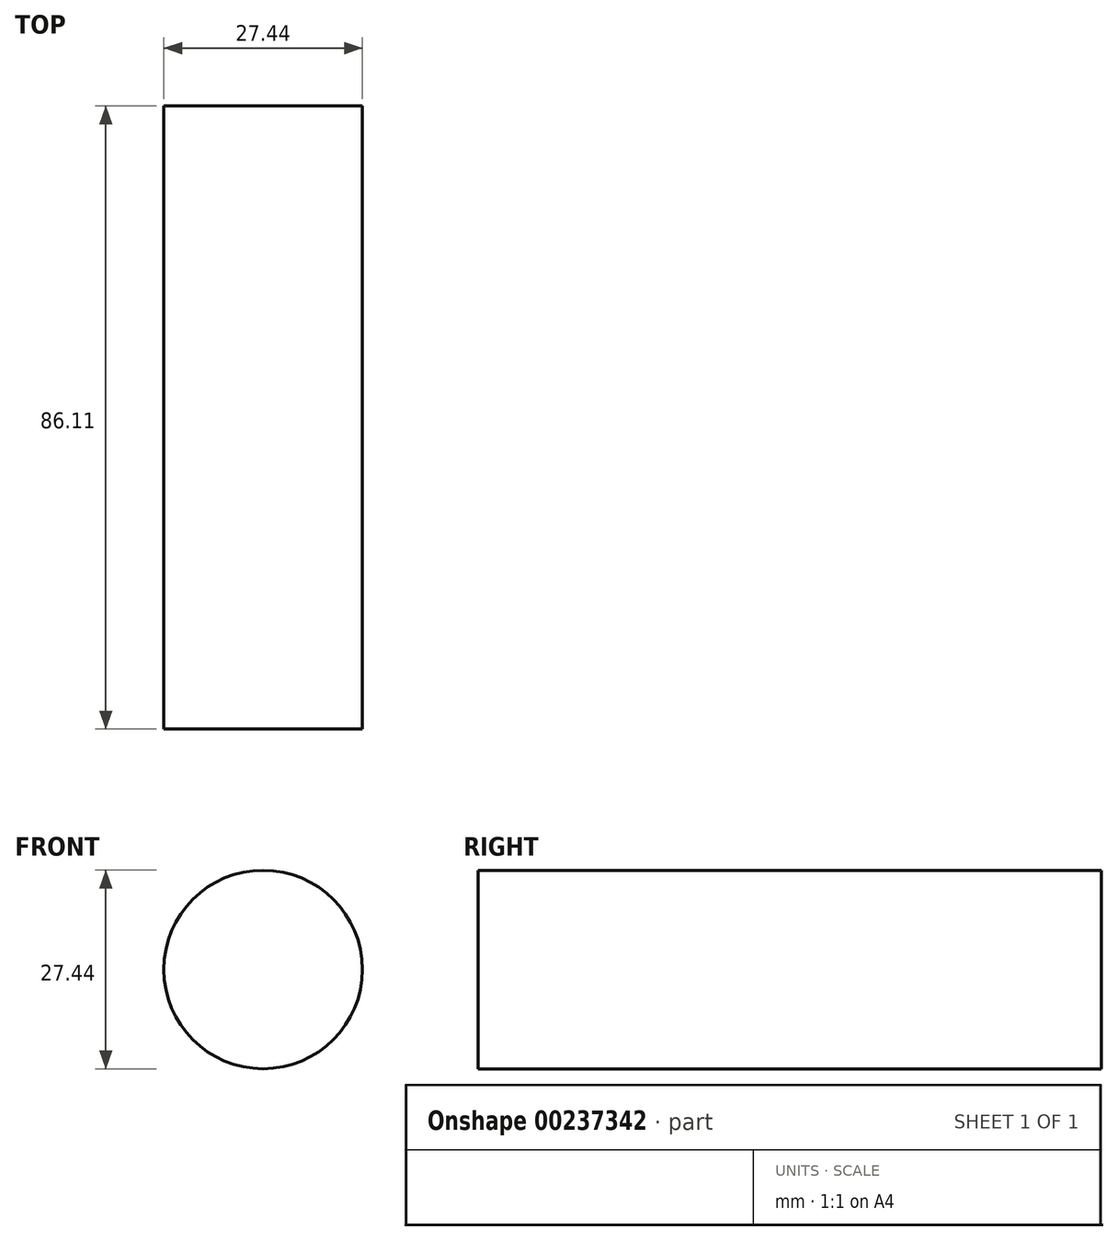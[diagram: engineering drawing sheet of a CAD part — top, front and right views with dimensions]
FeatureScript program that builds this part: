
annotation { "Feature Type Name" : "Feature", "Feature Type Description" : "" }
export const myFeature = defineFeature(function(context is Context, id is Id, definition is map)
    precondition{}
    {
        {
            var Q0;
            Q0=qCreatedBy(makeId("Front.planeOp"),FACE);
            var sketch = newSketch(context, id + "F0", { "sketchPlane" : qUnion([Q0])});
            skCircle(sketch, "E0", {"center": v(0, 0) * mm, "radius": 13.72 * mm});
            skSolve(sketch);
        }
        {
            var Q0;
            Q0 = qSketchRegion(id + "F0", true);
            extrude(context, id + "F1", {"entities" : qUnion([Q0]), "depth" : 86.1 * mm});
        }
    });
